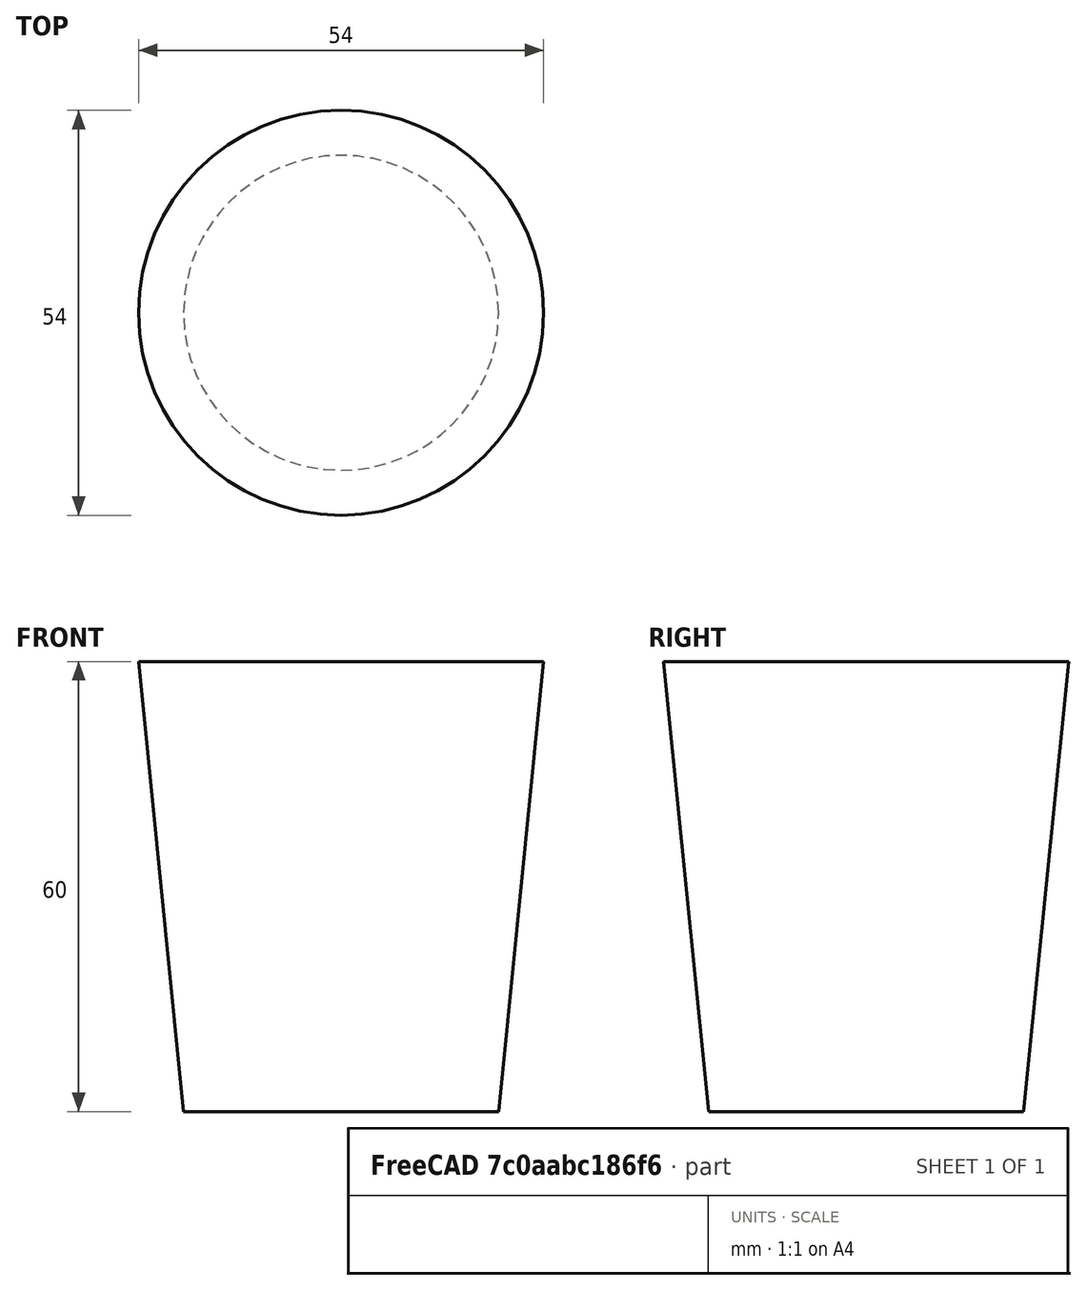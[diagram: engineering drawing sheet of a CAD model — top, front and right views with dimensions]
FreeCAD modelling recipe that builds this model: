
FCSTD DOCUMENT  (FreeCAD 0.18.3R)
Label: Trashcan_bottom
License: All rights reserved
LicenseURL: http://en.wikipedia.org/wiki/All_rights_reserved
objects: PartDesign::Body×2, Sketcher::SketchObject×1, PartDesign::Revolution×1
note: 5 computed .brp shape members not serialized (recipe doc carries the construction recipe); baked Part::Feature solids carry a one-line shape summary decoded from their .brp

FEATURE [PartDesign::Body] Body
  Origin = -> Origin
FEATURE [Sketcher::SketchObject] Sketch
  MapMode = 5
  Placement = pos=(0,0,0) rot=(1,0,0;1.5708rad)
  Support = -> [XZ_Plane001]
  sketch-geometry (4):
    g0: LineSegment StartX=0 StartY=0 StartZ=0 EndX=21 EndY=0 EndZ=0
    g1: LineSegment StartX=21 StartY=0 StartZ=0 EndX=27 EndY=60 EndZ=0
    g2: LineSegment StartX=27 StartY=60 StartZ=0 EndX=0 EndY=60 EndZ=0
    g3: LineSegment StartX=0 StartY=60 StartZ=0 EndX=0 EndY=0 EndZ=0
  constraints (11):
    c: Coincident(g-1,g0)
    c: Horizontal(g0)
    c: Coincident(g0,g1)
    c: Coincident(g1,g2)
    c: Horizontal(g2)
    c: Coincident(g2,g3)
    c: Coincident(g3,g0)
    c: Vertical(g3)
    c: DistanceX(g2,g2) = 27
    c: DistanceX(g0,g0) = 21
    c: DistanceY(g3,g3) = 60
FEATURE [PartDesign::Revolution] Revolution
  Angle = 360
  Axis = (0,2e-16,1)
  Base = (0,0,0)
  Placement = pos=(0,0,0) rot=(1,0,0;1.5708rad)
  Profile = -> Sketch
  ReferenceAxis = -> Sketch [V_Axis]
  Reversed = true
FEATURE [PartDesign::Body] Body001
  Group = -> [Sketch,Revolution]
  Origin = -> Origin001
  Tip = -> Revolution
